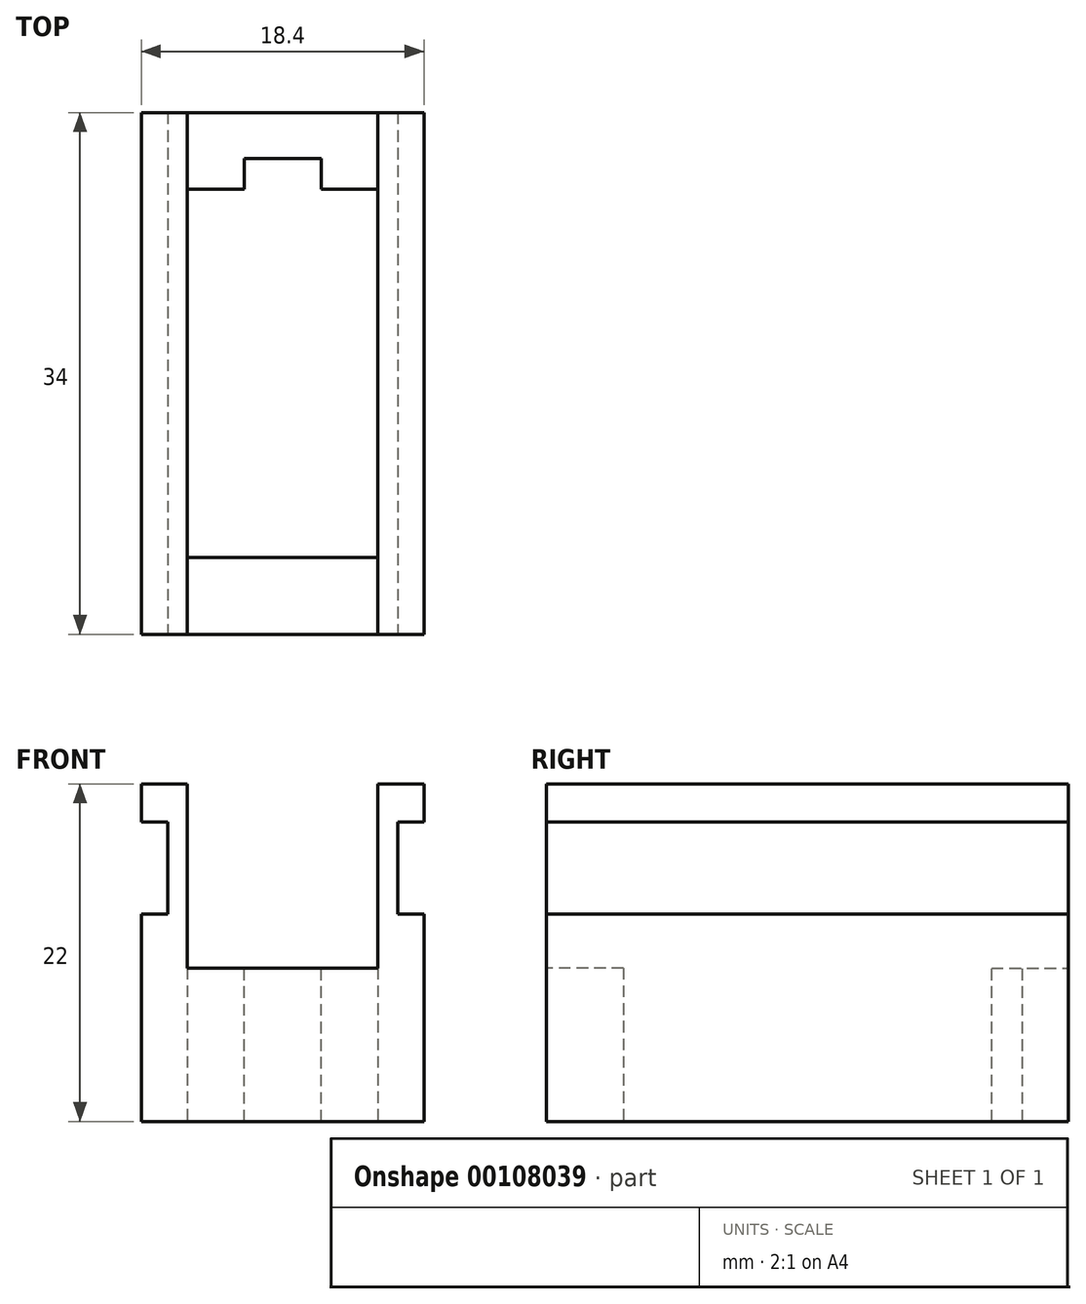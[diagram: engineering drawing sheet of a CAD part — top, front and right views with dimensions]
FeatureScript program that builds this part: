
annotation { "Feature Type Name" : "Feature", "Feature Type Description" : "" }
export const myFeature = defineFeature(function(context is Context, id is Id, definition is map)
    precondition{}
    {
        {
            var Q0;
            Q0=qCreatedBy(makeId("Right.planeOp"),FACE);
            var sketch = newSketch(context, id + "F0", { "sketchPlane" : qUnion([Q0])});
            skLineSegment(sketch, "E0.bottom", {"start": v(-11.5, 11.65) * mm, "end": v(11.5, 11.65) * mm});
            skLineSegment(sketch, "E0.top", {"start": v(-11.5, -11.65) * mm, "end": v(11.5, -11.65) * mm});
            skLineSegment(sketch, "E0.left", {"start": v(-11.5, 11.65) * mm, "end": v(-11.5, -11.65) * mm});
            skLineSegment(sketch, "E0.right", {"start": v(11.5, 11.65) * mm, "end": v(11.5, -11.65) * mm});
            skPoint(sketch, "E0.middle", {"position": v(0, 0) * mm});
            skSolve(sketch);
        }
        {
            var Q0;
            Q0=qCreatedBy(makeId("Right.planeOp"),FACE);
            var sketch = newSketch(context, id + "F1", { "sketchPlane" : qUnion([Q0])});
            skLineSegment(sketch, "E1.bottom", {"start": v(-17, 18.65) * mm, "end": v(-12, 18.65) * mm});
            skLineSegment(sketch, "E1.top", {"start": v(-17, -3.35) * mm, "end": v(-12, -3.35) * mm});
            skLineSegment(sketch, "E1.left", {"start": v(-17, 18.65) * mm, "end": v(-17, -3.35) * mm});
            skLineSegment(sketch, "E1.right", {"start": v(-12, 18.65) * mm, "end": v(-12, -3.35) * mm});
            skLineSegment(sketch, "E2", {"start": v(0, 0) * mm, "end": v(0, 13.9) * mm, "construction": true});
            skLineSegment(sketch, "E3.MirrorCS", {"start": v(12, 18.65) * mm, "end": v(12, -3.35) * mm});
            skLineSegment(sketch, "E4.MirrorCS", {"start": v(17, 18.65) * mm, "end": v(17, -3.35) * mm});
            skLineSegment(sketch, "E5.MirrorCS", {"start": v(17, 18.65) * mm, "end": v(12, 18.65) * mm});
            skLineSegment(sketch, "E6.MirrorCS", {"start": v(17, -3.35) * mm, "end": v(12, -3.35) * mm});
            skSolve(sketch);
        }
        {
            var Q0;
            Q0 = qSketchRegion(id + "F1", true);
            extrude(context, id + "F2", {"entities" : qUnion([Q0]), "endBound" : BoundingType.SYMMETRIC, "depth" : 12.4 * mm});
        }
        {
            var Q0;
            Q0=makeQuery(id+"F2.opExtrude","CAP_FACE",FACE,{"disambiguationData":[OSD([sQuery(id+"F1.wireOp",EDGE,"E1.bottom"),sQuery(id+"F1.wireOp",EDGE,"E1.top"),sQuery(id+"F1.wireOp",EDGE,"E1.left"),sQuery(id+"F1.wireOp",EDGE,"E1.right")])],"isStart":false});
            var sketch = newSketch(context, id + "F3", { "sketchPlane" : qUnion([Q0])});
            skLineSegment(sketch, "E7.bottom", {"start": v(-17, 18.65) * mm, "end": v(17, 18.65) * mm});
            skLineSegment(sketch, "E7.top", {"start": v(-17, -3.35) * mm, "end": v(17, -3.35) * mm});
            skLineSegment(sketch, "E7.left", {"start": v(-17, 18.65) * mm, "end": v(-17, -3.35) * mm});
            skLineSegment(sketch, "E7.right", {"start": v(17, 18.65) * mm, "end": v(17, -3.35) * mm});
            skSolve(sketch);
        }
        {
            var Q0;
            Q0 = qSketchRegion(id + "F3", true);
            extrude(context, id + "F4", {"entities" : qUnion([Q0]), "depth" : 3 * mm});
        }
        {
            var Q0;
            Q0=makeQuery(id+"F4.opExtrude","SWEPT_BODY",BODY,{"disambiguationData":[OSD([sQuery(id+"F3.wireOp",EDGE,"E7.bottom"),sQuery(id+"F3.wireOp",EDGE,"E7.top"),sQuery(id+"F3.wireOp",EDGE,"E7.left"),sQuery(id+"F3.wireOp",EDGE,"E7.right")])]});
            var Q1;
            Q1=qCreatedBy(makeId("Right.planeOp"),FACE);
            mirror(context, id + "F5", {"operationType" : NewBodyOperationType.ADD, "entities" : qUnion([Q0]), "mirrorPlane" : qUnion([Q1])});
        }
        {
            var Q0;
            {var subQ0=makeQuery(id+"F4.opExtrude","SWEPT_FACE",FACE,{"disambiguationData":[OSD([sQuery(id+"F3.wireOp",EDGE,"E7.bottom")])]});Q0=makeQuery(id+"F5.boolean.opBoolean","MERGE",FACE,{"derivedFrom":[makeQuery(id+"F2.opExtrude","SWEPT_FACE",FACE,{"disambiguationData":[OSD([sQuery(id+"F1.wireOp",EDGE,"E1.bottom")])]}),makeQuery(id+"F2.opExtrude","SWEPT_FACE",FACE,{"disambiguationData":[OSD([sQuery(id+"F1.wireOp",EDGE,"E5.MirrorCS")])]}),subQ0,makeQuery(id+"F5.opPattern","COPY",FACE,{"derivedFrom":subQ0,"instanceName":"1"})]});}
            var sketch = newSketch(context, id + "F6", { "sketchPlane" : qUnion([Q0])});
            skLineSegment(sketch, "E8.bottom", {"start": v(-6.2, -12) * mm, "end": v(6.2, -12) * mm});
            skLineSegment(sketch, "E8.top", {"start": v(-6.2, -17) * mm, "end": v(6.2, -17) * mm});
            skLineSegment(sketch, "E8.left", {"start": v(-6.2, -12) * mm, "end": v(-6.2, -17) * mm});
            skLineSegment(sketch, "E8.right", {"start": v(6.2, -12) * mm, "end": v(6.2, -17) * mm});
            skLineSegment(sketch, "E9", {"start": v(0, 0.43) * mm, "end": v(0, -12) * mm, "construction": true});
            skLineSegment(sketch, "E10", {"start": v(0, 0) * mm, "end": v(11.58, 0) * mm, "construction": true});
            skLineSegment(sketch, "E11.MirrorCS", {"start": v(-6.2, 12) * mm, "end": v(-6.2, 17) * mm});
            skLineSegment(sketch, "E12.MirrorCS", {"start": v(-6.2, 12) * mm, "end": v(6.2, 12) * mm});
            skLineSegment(sketch, "E13.MirrorCS", {"start": v(-6.2, 17) * mm, "end": v(6.2, 17) * mm});
            skLineSegment(sketch, "E14.MirrorCS", {"start": v(6.2, 12) * mm, "end": v(6.2, 17) * mm});
            skSolve(sketch);
        }
        {
            var Q0;
            Q0 = qSketchRegion(id + "F6", true);
            extrude(context, id + "F7", {"entities" : qUnion([Q0]), "operationType" : NewBodyOperationType.REMOVE, "oppositeDirection" : true, "depth" : 12 * mm});
        }
        {
            var Q0;
            Q0=makeQuery(id+"F7.boolean.opBoolean","COPY",FACE,{"derivedFrom":makeQuery(id+"F7.opExtrude","CAP_FACE",FACE,{"disambiguationData":[OSD([sQuery(id+"F6.wireOp",EDGE,"E11.MirrorCS"),sQuery(id+"F6.wireOp",EDGE,"E12.MirrorCS"),sQuery(id+"F6.wireOp",EDGE,"E13.MirrorCS"),sQuery(id+"F6.wireOp",EDGE,"E14.MirrorCS")])],"isStart":false})});
            var sketch = newSketch(context, id + "F8", { "sketchPlane" : qUnion([Q0])});
            skLineSegment(sketch, "E15.bottom", {"start": v(-2.5, 12) * mm, "end": v(2.5, 12) * mm});
            skLineSegment(sketch, "E15.top", {"start": v(-2.5, 14) * mm, "end": v(2.5, 14) * mm});
            skLineSegment(sketch, "E15.left", {"start": v(-2.5, 12) * mm, "end": v(-2.5, 14) * mm});
            skLineSegment(sketch, "E15.right", {"start": v(2.5, 12) * mm, "end": v(2.5, 14) * mm});
            skPoint(sketch, "E16", {"position": v(0, 12) * mm});
            skSolve(sketch);
        }
        {
            var Q0;
            Q0 = qSketchRegion(id + "F8", true);
            extrude(context, id + "F9", {"entities" : qUnion([Q0]), "operationType" : NewBodyOperationType.REMOVE, "oppositeDirection" : true, "depth" : 25 * mm});
        }
        {
            var Q0;
            {var subQ0=makeQuery(id+"F4.opExtrude","SWEPT_FACE",FACE,{"disambiguationData":[OSD([sQuery(id+"F3.wireOp",EDGE,"E7.left")])]});Q0=makeQuery(id+"F5.boolean.opBoolean","MERGE",FACE,{"derivedFrom":[makeQuery(id+"F2.opExtrude","SWEPT_FACE",FACE,{"disambiguationData":[OSD([sQuery(id+"F1.wireOp",EDGE,"E1.left")])]}),subQ0,makeQuery(id+"F5.opPattern","COPY",FACE,{"derivedFrom":subQ0,"instanceName":"1"})]});}
            var sketch = newSketch(context, id + "F10", { "sketchPlane" : qUnion([Q0])});
            skLineSegment(sketch, "E17.bottom", {"start": v(-9.2, 16.15) * mm, "end": v(-7.5, 16.15) * mm});
            skLineSegment(sketch, "E17.top", {"start": v(-9.2, 10.15) * mm, "end": v(-7.5, 10.15) * mm});
            skLineSegment(sketch, "E17.left", {"start": v(-9.2, 16.15) * mm, "end": v(-9.2, 10.15) * mm});
            skLineSegment(sketch, "E17.right", {"start": v(-7.5, 16.15) * mm, "end": v(-7.5, 10.15) * mm});
            skLineSegment(sketch, "E18", {"start": v(0, 0) * mm, "end": v(0, 17.7) * mm, "construction": true});
            skPoint(sketch, "E18.endSnap0", {"position": v(0, 6.65) * mm});
            skLineSegment(sketch, "E19.MirrorCS", {"start": v(9.2, 16.15) * mm, "end": v(7.5, 16.15) * mm});
            skLineSegment(sketch, "E20.MirrorCS", {"start": v(7.5, 16.15) * mm, "end": v(7.5, 10.15) * mm});
            skLineSegment(sketch, "E21.MirrorCS", {"start": v(9.2, 16.15) * mm, "end": v(9.2, 10.15) * mm});
            skLineSegment(sketch, "E22.MirrorCS", {"start": v(9.2, 10.15) * mm, "end": v(7.5, 10.15) * mm});
            skSolve(sketch);
        }
        {
            var Q0;
            Q0 = qSketchRegion(id + "F10", true);
            extrude(context, id + "F11", {"entities" : qUnion([Q0]), "operationType" : NewBodyOperationType.REMOVE, "endBound" : BoundingType.THROUGH_ALL, "oppositeDirection" : true, "depth" : 25 * mm});
        }
    });
